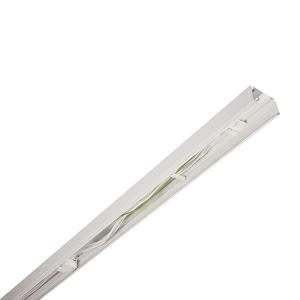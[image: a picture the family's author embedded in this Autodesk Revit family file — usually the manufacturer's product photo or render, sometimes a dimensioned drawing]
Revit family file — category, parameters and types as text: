
# Revit family: 3f_filippi_-_3f_linux_s_ip40_3f_filippi_-_a20026_-_3f_linux_s_7p_l1778
name_source: partatom
category: Lighting Fixtures
units: mm (PartAtom-declared; Revit-internal decimal feet)

## family parameters
Cut with Voids When Loaded = No
Host = Face
Light Source = No
Part Type = Normal
Room Calculation Point = No
Round Connector Dimension = Use Diameter
Shared = No

## types (1)
- 3F Filippi - 3F Linux S IP40
    Apparent Load = 0 VA
    Default Elevation = 1800 mm
    Description = Wired supporting structure for continuous channels, suitable for: lighting units 3F Linux L, 3F Linux D, 3F Linux DR, other luminaires or transport of electrical lines.

MECHANICAL
Wired base in hot galvanised steel and painted with polyester base in white colour, obtained through rolling process.
Saline-mist resistance equal to 500hrs and damp resistance equal to 700hrs.
Dimensions: 1778x62 mm, height 38 mm. Weight 2.01 kg.
IP40 protection degree.
Glow-wire test resistance 850°C.

ELECTRICAL
7-pole through power supply line with with H07Z-U Halogen Free cables (2.5 mm² HT90 cross-section), equipped with quick connection start/end channel terminal blocks, non-reversible, 1 power supply pedestal.

INSTALLATION
Ceiling / Suspended / Wall.
All accessories dedicated to this product are available on the Catalog and on our website www.3F-Filippi.com.

APPLICATIONS
Environments: commercial, exhibition areas, transit areas, lobbies or waiting rooms, shops, schools.

WARNING
Luminaire designed for disposal/recycling at end-of-life.
    Height = 38 mm
    Lamp = 0 x
    Length = 1778 mm
    Luminous efficacy = 0 lm/W
    Manufacturer = 3F Filippi
    ModVariant = No
    Model = 3F Filippi - A20026 - 3F Linux S 7P L1778
    Mounting Place = Ceiling
    Mounting Type = Pendant
    Number of Poles = 1
    OnlyDefault = Yes
    Power Factor = 1
    Product Name = 3F Filippi - 3F Linux S IP40
    Product group = Accessories
    ProductGroupID = 98
    Protection Class = Protection class
    Protection Degree = IP 40
    RLX_Detail_Level = 1
    RLX_Emergency_Light_Flux = 0 lm
    RLX_Emergency_Type = 0
    RLX_Emergency_Type_DB = No
    RlxData = <blob elided: 32437 chars, md5=687f45c1>
    Standby Power = 0 W
    System Light Flux = 0 lm
    System Power = 0 W
    Type Comments = Product without accessories
    Type Image = 3ffilippi_3f_linux_s_ip40_l1778.jpg
    URL = http://relux.com
    VarID = ---
    Voltage = 0 V
    Weight = 0.00 kg
    Width = 62 mm  [stored 0.203412 ft]

note: [stored X ft] marks values corroborated as IEEE doubles in the binary element streams (Revit-internal decimal feet)

## geometry (parser evidence)
native form markers: Blend x4, Sweep x10
no freeform markers — native parametric forms only
